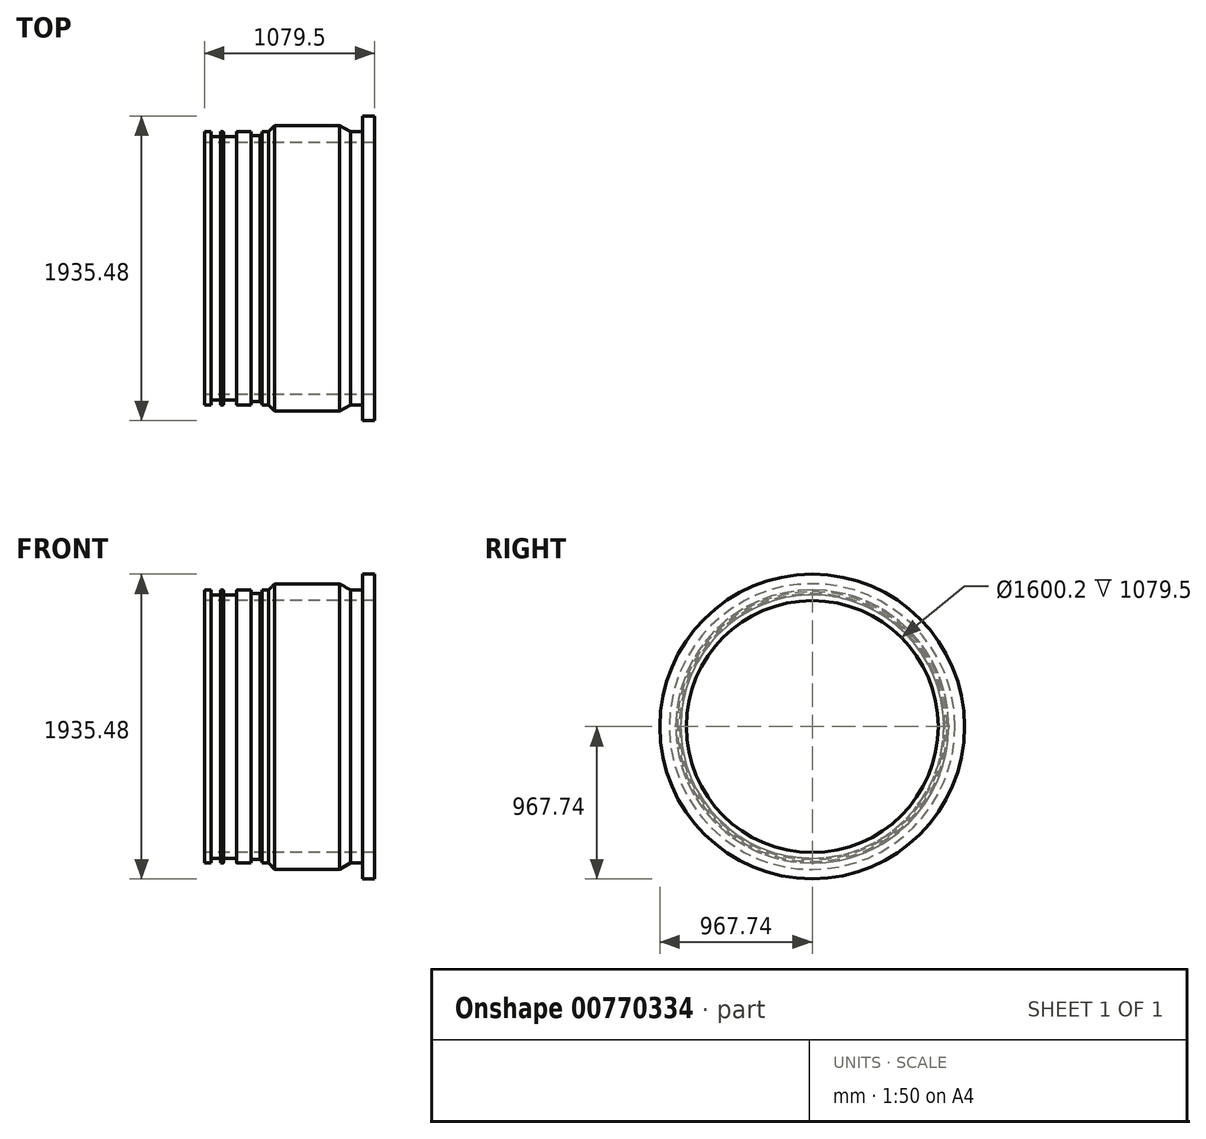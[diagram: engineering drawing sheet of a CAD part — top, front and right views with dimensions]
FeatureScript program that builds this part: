
annotation { "Feature Type Name" : "Feature", "Feature Type Description" : "" }
export const myFeature = defineFeature(function(context is Context, id is Id, definition is map)
    precondition{}
    {
        {
            var Q0;
            Q0=qCreatedBy(makeId("Front.planeOp"),FACE);
            var sketch = newSketch(context, id + "F0", { "sketchPlane" : qUnion([Q0])});
            skLineSegment(sketch, "E0", {"start": v(0, 0) * mm, "end": v(1672.14, 0) * mm, "construction": true});
            skLineSegment(sketch, "E1", {"start": v(0, 867.4) * mm, "end": v(41.66, 867.4) * mm});
            skLineSegment(sketch, "E2", {"start": v(41.66, 867.4) * mm, "end": v(41.66, 835.79) * mm});
            skLineSegment(sketch, "E3", {"start": v(41.66, 835.79) * mm, "end": v(101.6, 835.79) * mm});
            skLineSegment(sketch, "E4", {"start": v(101.6, 835.79) * mm, "end": v(101.6, 867.4) * mm});
            skLineSegment(sketch, "E5", {"start": v(101.6, 867.4) * mm, "end": v(119.09, 867.4) * mm});
            skLineSegment(sketch, "E6", {"start": v(119.09, 867.4) * mm, "end": v(119.09, 835.79) * mm});
            skLineSegment(sketch, "E7", {"start": v(119.09, 835.79) * mm, "end": v(203.2, 835.79) * mm});
            skLineSegment(sketch, "E8", {"start": v(203.2, 835.79) * mm, "end": v(203.2, 867.4) * mm});
            skLineSegment(sketch, "E9", {"start": v(203.2, 867.4) * mm, "end": v(294.64, 867.4) * mm});
            skLineSegment(sketch, "E10", {"start": v(294.64, 867.4) * mm, "end": v(294.64, 844.55) * mm});
            skLineSegment(sketch, "E11", {"start": v(294.64, 844.55) * mm, "end": v(365.76, 844.55) * mm});
            skLineSegment(sketch, "E12", {"start": v(365.76, 844.55) * mm, "end": v(365.76, 867.4) * mm});
            skLineSegment(sketch, "E13", {"start": v(365.76, 867.4) * mm, "end": v(406.4, 867.4) * mm});
            skLineSegment(sketch, "E14", {"start": v(406.4, 867.4) * mm, "end": v(446.28, 907.29) * mm});
            skLineSegment(sketch, "E15", {"start": v(446.28, 907.29) * mm, "end": v(858.03, 907.29) * mm});
            skLineSegment(sketch, "E16", {"start": v(1079.5, 967.74) * mm, "end": v(1079.5, 800.1) * mm});
            skLineSegment(sketch, "E17", {"start": v(1079.5, 800.1) * mm, "end": v(0, 800.1) * mm});
            skLineSegment(sketch, "E18", {"start": v(0, 800.1) * mm, "end": v(0, 867.4) * mm});
            skLineSegment(sketch, "E19", {"start": v(858.03, 907.29) * mm, "end": v(927.1, 867.4) * mm});
            skLineSegment(sketch, "E20", {"start": v(927.1, 867.41) * mm, "end": v(1003.3, 867.41) * mm});
            skLineSegment(sketch, "E21", {"start": v(1003.3, 867.41) * mm, "end": v(1003.3, 967.74) * mm});
            skLineSegment(sketch, "E22", {"start": v(1003.3, 967.74) * mm, "end": v(1079.5, 967.74) * mm});
            skSolve(sketch);
        }
        {
            var Q0;
            Q0=makeQuery(id+"F0.imprint","IMPRINT",FACE,{"disambiguationData":[TD([[makeQuery(id+"F0.imprint","IMPRINT",EDGE,{"derivedFrom":sQuery(id+"F0.wireOp",EDGE,"E1")}),-1.0]])]});
            var Q1;
            Q1=sQuery(id+"F0.wireOp",EDGE,"E0");
            revolve(context, id + "F1", {"surfaceOperationType" : NewSurfaceOperationType.NEW, "entities" : qUnion([Q0]), "axis" : qUnion([Q1]), "revolveType" : RevolveType.FULL});
        }
        {
            var Q0;
            Q0=makeQuery(id+"F1.opRevolve","SWEPT_EDGE",EDGE,{"disambiguationData":[OSD([sQuery(id+"F0.wireOp",EDGE,"E8"),sQuery(id+"F0.wireOp",EDGE,"E9")])]});
            var Q1;
            Q1=makeQuery(id+"F1.opRevolve","SWEPT_EDGE",EDGE,{"disambiguationData":[OSD([sQuery(id+"F0.wireOp",EDGE,"E7"),sQuery(id+"F0.wireOp",EDGE,"E8")])]});
            var Q2;
            Q2=makeQuery(id+"F1.opRevolve","SWEPT_EDGE",EDGE,{"disambiguationData":[OSD([sQuery(id+"F0.wireOp",EDGE,"E5"),sQuery(id+"F0.wireOp",EDGE,"E6")])]});
            var Q3;
            Q3=makeQuery(id+"F1.opRevolve","SWEPT_EDGE",EDGE,{"disambiguationData":[OSD([sQuery(id+"F0.wireOp",EDGE,"E6"),sQuery(id+"F0.wireOp",EDGE,"E7")])]});
            fillet(context, id + "F2", {"entities" : qUnion([Q0, Q1, Q2, Q3]), "radius" : 3.3 * mm, "tangentPropagation" : true, "allowEdgeOverflow" : false});
        }
        {
            var Q0;
            Q0=makeQuery(id+"F1.opRevolve","SWEPT_EDGE",EDGE,{"disambiguationData":[OSD([sQuery(id+"F0.wireOp",EDGE,"E11"),sQuery(id+"F0.wireOp",EDGE,"E12")])]});
            chamfer(context, id + "F3", {"entities" : qUnion([Q0]), "width" : 12.7 * mm, "tangentPropagation" : true});
        }
    });
